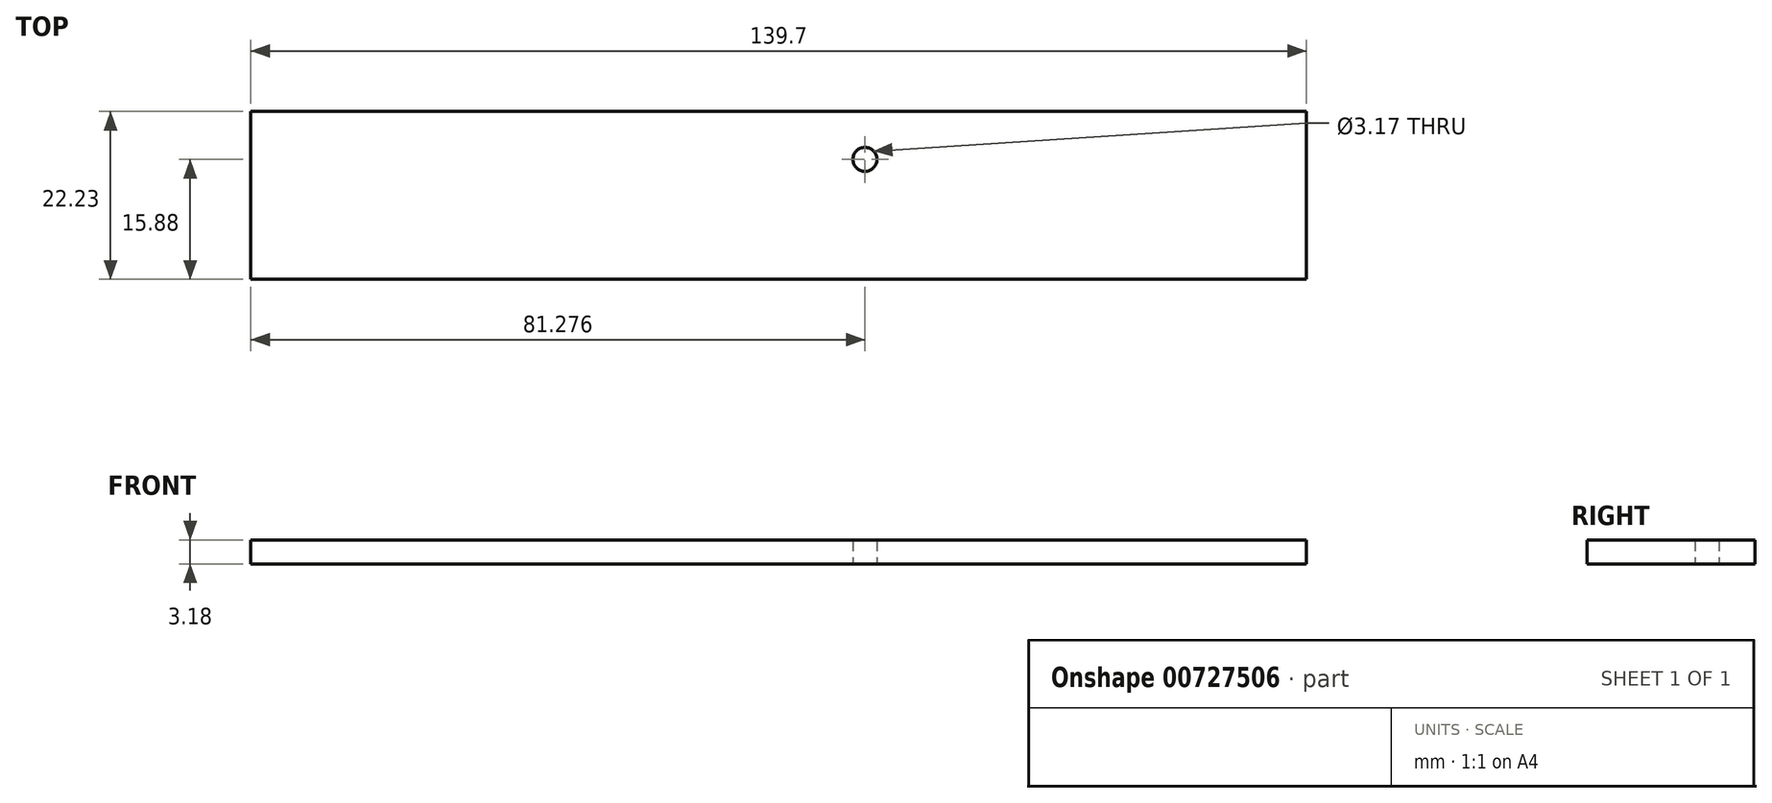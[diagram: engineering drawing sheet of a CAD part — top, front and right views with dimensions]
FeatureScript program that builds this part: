
annotation { "Feature Type Name" : "Feature", "Feature Type Description" : "" }
export const myFeature = defineFeature(function(context is Context, id is Id, definition is map)
    precondition{}
    {
        {
            var Q0;
            Q0=qCreatedBy(makeId("Top.planeOp"),FACE);
            var sketch = newSketch(context, id + "F0", { "sketchPlane" : qUnion([Q0])});
            skLineSegment(sketch, "E0.bottom", {"start": v(-101.9, 12.7) * mm, "end": v(25.1, 12.7) * mm});
            skLineSegment(sketch, "E0.top", {"start": v(-101.9, -9.52) * mm, "end": v(25.1, -9.52) * mm});
            skLineSegment(sketch, "E1", {"start": v(25.1, 12.7) * mm, "end": v(25.1, -9.52) * mm});
            skCircle(sketch, "E2", {"center": v(-33.31, 6.35) * mm, "radius": 1.59 * mm});
            skLineSegment(sketch, "E3", {"start": v(-101.9, 12.7) * mm, "end": v(-114.6, 12.7) * mm});
            skLineSegment(sketch, "E4", {"start": v(-114.6, -9.53) * mm, "end": v(-101.9, -9.53) * mm});
            skLineSegment(sketch, "E5", {"start": v(-114.6, 12.7) * mm, "end": v(-114.6, -9.53) * mm});
            skSolve(sketch);
        }
        {
            var Q0;
            Q0=makeQuery(id+"F0.imprint","IMPRINT",FACE,{"disambiguationData":[TD([[makeQuery(id+"F0.imprint","IMPRINT",EDGE,{"derivedFrom":sQuery(id+"F0.wireOp",EDGE,"E0.bottom")}),-1.0]])]});
            extrude(context, id + "F1", {"entities" : qUnion([Q0]), "depth" : 3.17 * mm, "offsetDistance" : 25.4 * mm});
        }
    });
